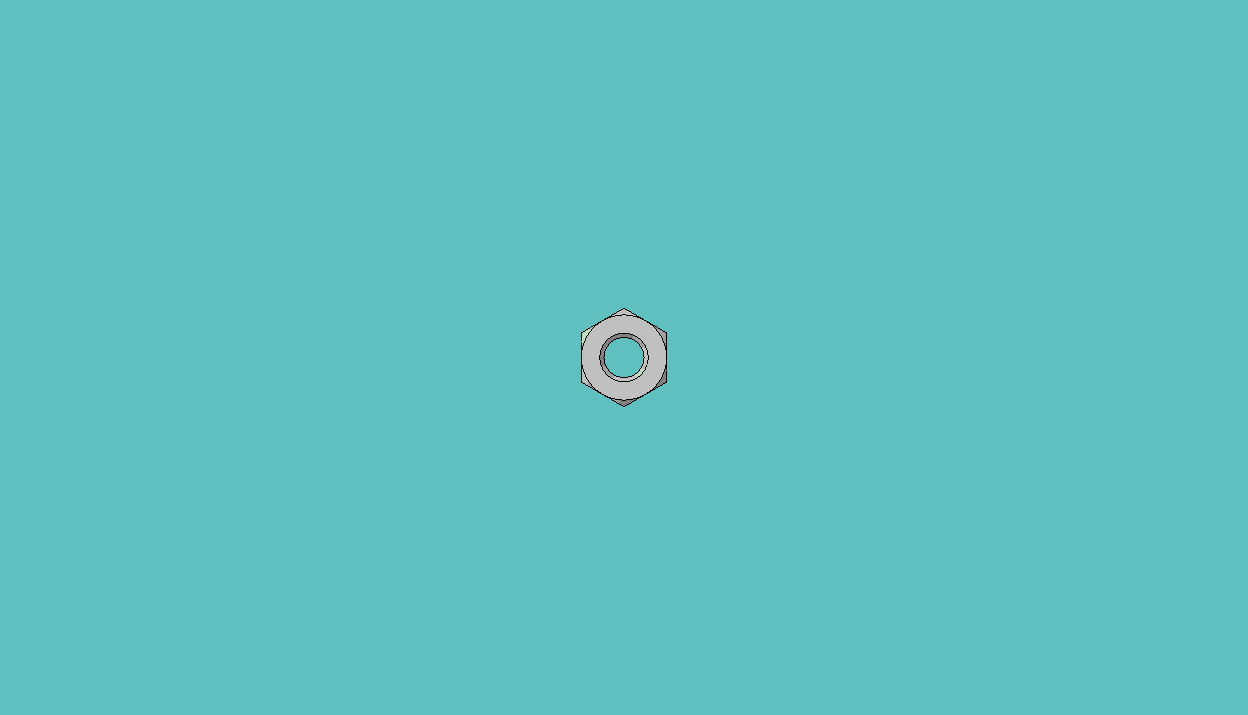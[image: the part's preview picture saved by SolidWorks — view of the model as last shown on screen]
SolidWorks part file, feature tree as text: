
SOLIDWORKS PART (.sldprt)
format: sldprt  version: not decoded by parser v0  size: 211,456 bytes
history: native  units: mm
features: sketch x5, cut_revolve x4, plane x3, material x1, extrude x1, thread x1, pattern_linear x1 + 2 further entries (+11 scaffold rows collapsed; 1 parser-record rows omitted)
feature tree (30):
  scaffold x11  (default folders/planes/origin — collapsed)
  material  "Material <not specified>"
  plane  "Plane1"
  plane  "Plane2"
  plane  "Plane3"
  parser-record x1  (decoder bookkeeping rows leaked as tree rows — omitted from the tree; the rows remain in map.json)
  cut_revolve  "EndChamfer"  [1 undecoded]
  sketch  "Sketch5"
  extrude  "BaseNut"  [1 undecoded]
  sketch  "BaseNutSke"  dims[c1.Tap_drill=3.3mm c1.D1=50.8mm c2.D1=30.0deg c2.D2=~24.797543mm c3.D2=60.0deg c3.D3=50.8mm c4.D3=30.0deg c4.D4=~24.797543mm c5.D4=60.0deg c6.D4=~24.797543mm c7.D4=60.0deg c8.D4=~24.797543mm c9.D4=60.0deg c9.Width_flats=7.0mm c9.D1=~21.475302mm c9.D2=~21.475302mm c10.D1=~21.475302mm c10.D2=3.5mm c10.D3=3.5mm c11.D1=~24.797543mm c12.D1=120.0deg c13.D1=~23.397294mm c14.D1=120.0deg c14.D4=3.5mm]
  thread  "ThreadCosmetic"  Diameter=4mm Thread_major=4mm Thickness=3.2mm  [1 undecoded]
  pattern_linear  "ThdSchPat"  [2 undecoded]
  cut_revolve  "ThreadSchematic"  [1 undecoded]
  sketch  "ThdSchSke"  dims[c1.D1=~4.490128mm c2.D1=90.0deg c3.D1=~4.490128mm c3.VeeAngle=70.0deg c4.D1=19.5834mm c4.SideAngle=55.0deg c5.D1=~4.490128mm c5.SideAngle=55.0deg c5.ThreadDepth=2.54mm c6.ThreadDepth=3.175mm c6.Thread_Major=6.35mm c6.D1=~9.573347mm c6.D2=~9.428305mm c6.OverCut=1.65mm c6.Tap_Drill=3.3mm c6.Advance=1.27mm c6.Thread_major=4.0mm c7.Advance=0.7mm c7.D1=6.35mm c7.D2=0.0254mm c8.D1=0.0254mm c9.D1=360.0deg c9.Num_threads=6.0 c9.Advance=~0.62984mm c9.D2=1.0 c9.D4=50.0mm c10.D1=~8.980256mm c11.D1=315.0deg c12.D1=~8.980256mm c13.D1=45.0deg c13.D2=~8.94581mm c14.D2=~1.952549deg c14.D3=6.35mm c15.D2=25.7048mm c15.D1=~6.352235mm c16.D1=35.0deg c16.D2=12.7mm c16.D3=12.7mm c17.D2=22.5552mm c17.D3=25.4mm c17.D4=12.7mm c18.D3=12.7mm c18.D2=0.0508mm c18.Offset1=25.4254mm c18.ThreadMajor=12.7mm c18.ChamferDepth=0.385mm c18.Offset2=3.2762mm c19.ThreadMajor=2.0mm c19.Offset1=3.2254mm c19.D1=360.0deg]
  sketch  "Sketch4"  dims[c1.D1=38.1mm c1.Bearing_ht=0.4mm c1.D3=12.7mm c1.D4=10.0mm c1.D5=2.54mm c1.D6=18.8722mm c2.D3=10.0mm c2.D1=3.5mm c2.D2=~3.890588mm c3.D2=~139.242599deg c4.D2=22.5298mm c5.D2=45.0deg c6.D2=~10.392305mm c7.D2=30.0deg]
  cut_revolve  "Bearing-Face"  Angle=360deg
  sketch  "Sketch3"  dims[c1.D1=3.5mm c1.D2=2.4mm c1.D3=12.7mm c1.D4=10.0mm c1.D5=10.9093mm c1.D6=~10.998523mm c2.D6=~179.413404deg c3.D6=~2.539714mm c3.D3=10.0mm c3.D5=9.525mm c3.D2=~10.392305mm c4.D2=30.0deg]
  cut_revolve  "Double-Chamfer"  Angle=360deg
  "ConfigurationName"  CopiedFlag=1
  "ConfigurationName"  CopiedFlag=0
decode coverage: 7 of 12 modeling features carry decoded parameters; 2 rows unclassified (native names shown)
note: ~ marks probable driven/reference dimensions
note: 6 parameter values undecoded
summary: no parameter record found for 3 features
note: suppression state not decoded; provenance and decode notes live in map.json
